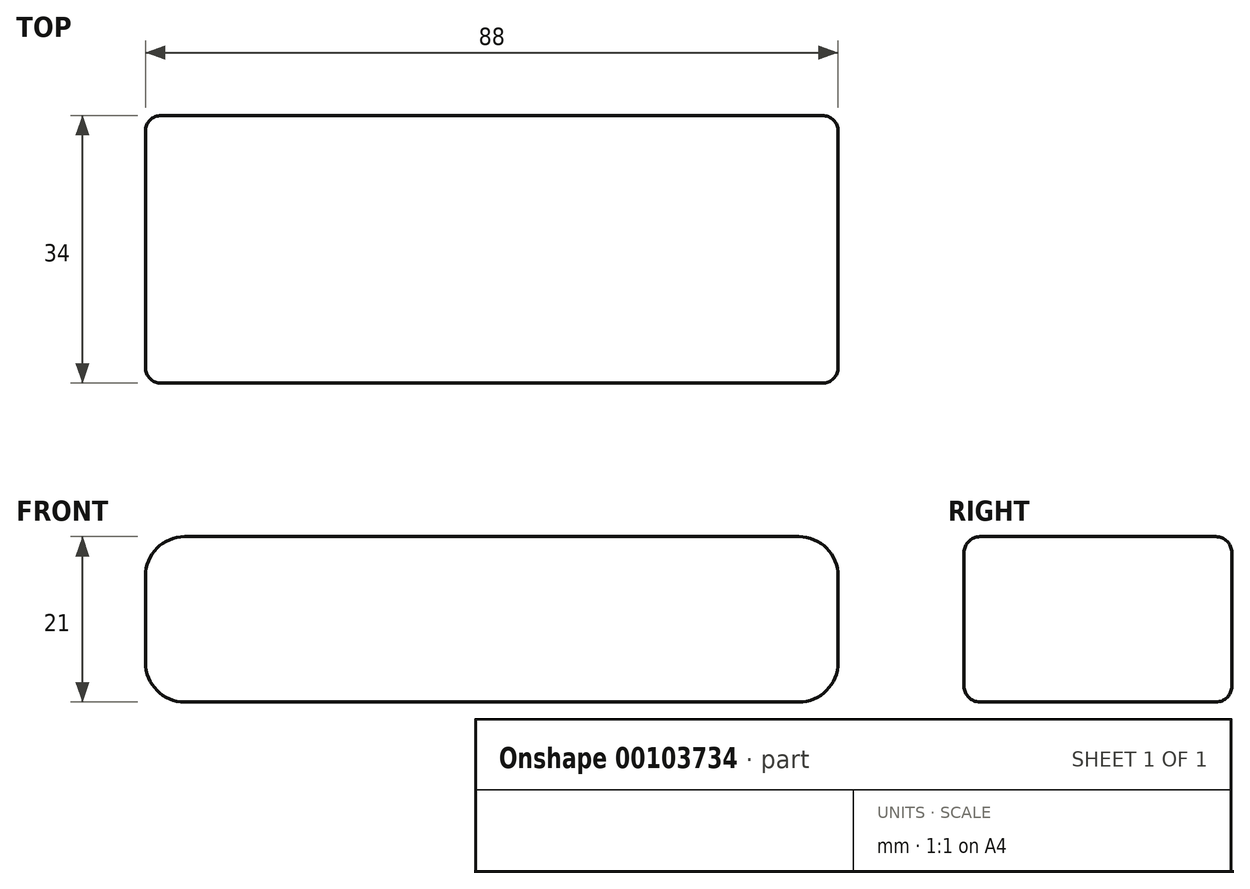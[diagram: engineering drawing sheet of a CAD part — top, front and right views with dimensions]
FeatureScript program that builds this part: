
annotation { "Feature Type Name" : "Feature", "Feature Type Description" : "" }
export const myFeature = defineFeature(function(context is Context, id is Id, definition is map)
    precondition{}
    {
        {
            var Q0;
            Q0=qCreatedBy(makeId("Top.planeOp"),FACE);
            var sketch = newSketch(context, id + "F0", { "sketchPlane" : qUnion([Q0])});
            skLineSegment(sketch, "E0.bottom", {"start": v(44, -17) * mm, "end": v(-44, -17) * mm});
            skLineSegment(sketch, "E0.top", {"start": v(44, 17) * mm, "end": v(-44, 17) * mm});
            skLineSegment(sketch, "E0.left", {"start": v(44, -17) * mm, "end": v(44, 17) * mm});
            skLineSegment(sketch, "E0.right", {"start": v(-44, -17) * mm, "end": v(-44, 17) * mm});
            skPoint(sketch, "E0.middle", {"position": v(0, 0) * mm});
            skSolve(sketch);
        }
        {
            var Q0;
            Q0=makeQuery(id+"F0.imprint","IMPRINT",FACE,{"disambiguationData":[TD([[makeQuery(id+"F0.imprint","IMPRINT",EDGE,{"derivedFrom":sQuery(id+"F0.wireOp",EDGE,"E0.bottom")}),-1.0]])]});
            extrude(context, id + "F1", {"entities" : qUnion([Q0]), "depth" : 21 * mm});
        }
        {
            var Q0;
            Q0=makeQuery(id+"F1.opExtrude","CAP_EDGE",EDGE,{"disambiguationData":[OSD([sQuery(id+"F0.wireOp",EDGE,"E0.bottom")])],"isStart":false});
            var Q1;
            Q1=makeQuery(id+"F1.opExtrude","CAP_EDGE",EDGE,{"disambiguationData":[OSD([sQuery(id+"F0.wireOp",EDGE,"E0.bottom")])],"isStart":true});
            var Q2;
            Q2=makeQuery(id+"F1.opExtrude","CAP_EDGE",EDGE,{"disambiguationData":[OSD([sQuery(id+"F0.wireOp",EDGE,"E0.top")])],"isStart":false});
            var Q3;
            Q3=makeQuery(id+"F1.opExtrude","CAP_EDGE",EDGE,{"disambiguationData":[OSD([sQuery(id+"F0.wireOp",EDGE,"E0.top")])],"isStart":true});
            var Q4;
            Q4=makeQuery(id+"F1.opExtrude","SWEPT_EDGE",EDGE,{"disambiguationData":[OSD([sQuery(id+"F0.wireOp",EDGE,"E0.top"),sQuery(id+"F0.wireOp",EDGE,"E0.right")])]});
            var Q5;
            Q5=makeQuery(id+"F1.opExtrude","SWEPT_EDGE",EDGE,{"disambiguationData":[OSD([sQuery(id+"F0.wireOp",EDGE,"E0.bottom"),sQuery(id+"F0.wireOp",EDGE,"E0.right")])]});
            var Q6;
            Q6=makeQuery(id+"F1.opExtrude","SWEPT_EDGE",EDGE,{"disambiguationData":[OSD([sQuery(id+"F0.wireOp",EDGE,"E0.top"),sQuery(id+"F0.wireOp",EDGE,"E0.left")])]});
            var Q7;
            Q7=makeQuery(id+"F1.opExtrude","SWEPT_EDGE",EDGE,{"disambiguationData":[OSD([sQuery(id+"F0.wireOp",EDGE,"E0.bottom"),sQuery(id+"F0.wireOp",EDGE,"E0.left")])]});
            fillet(context, id + "F2", {"entities" : qUnion([Q0, Q1, Q2, Q3, Q4, Q5, Q6, Q7]), "radius" : 2 * mm, "tangentPropagation" : true, "allowEdgeOverflow" : false});
        }
        {
            var Q0;
            Q0=makeQuery(id+"F1.opExtrude","CAP_EDGE",EDGE,{"disambiguationData":[OSD([sQuery(id+"F0.wireOp",EDGE,"E0.left")])],"isStart":true});
            var Q1;
            Q1=makeQuery(id+"F1.opExtrude","CAP_EDGE",EDGE,{"disambiguationData":[OSD([sQuery(id+"F0.wireOp",EDGE,"E0.left")])],"isStart":false});
            var Q2;
            Q2=makeQuery(id+"F1.opExtrude","CAP_EDGE",EDGE,{"disambiguationData":[OSD([sQuery(id+"F0.wireOp",EDGE,"E0.right")])],"isStart":true});
            var Q3;
            Q3=makeQuery(id+"F1.opExtrude","CAP_EDGE",EDGE,{"disambiguationData":[OSD([sQuery(id+"F0.wireOp",EDGE,"E0.right")])],"isStart":false});
            fillet(context, id + "F3", {"entities" : qUnion([Q0, Q1, Q2, Q3]), "radius" : 5 * mm, "tangentPropagation" : true, "allowEdgeOverflow" : false});
        }
    });
